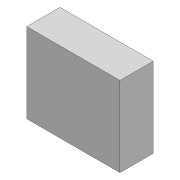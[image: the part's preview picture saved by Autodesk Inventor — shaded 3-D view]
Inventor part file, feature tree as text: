
AUTODESK INVENTOR PART (.ipt)
format: ipt  version: 2018 (Build 220112000, 112)  size: 128,512 bytes
history: native  units: mm
features: extrude x2, mirror x2, sketch x2, fillet x1
ambient origin geometry x8: Origin, YZ Plane, XZ Plane, XY Plane, X Axis, Y Axis, Z Axis, Center Point
bodies: Solid1 (feature_tree)
feature tree (7):
  extrude  "Extrusion1"  Depth=14.0mm
  extrude  "Extrusion2"  Depth=0.25mm
  mirror  "Mirror1"
  mirror  "Mirror2"
  fillet  "Fillet1"  Radius=4.88mm
  sketch  "Sketch1"  dims[d0=12.0mm d1=14.0mm]
  sketch  "Sketch2"  dims[d2=4.17mm d3=2.54mm d4=4.88mm d6=1.6mm d7=1.6mm d8=5.0mm d9=0.0mm d10=0.5mm d11=2.0mm d12=0.0mm d13=0.25mm]
